# Revit family: QF_BOURGEAT_silo_encastrable_modele_rond_assiettes260
name_source: partatom
category: Equipement spécialisé
revit_build: Autodesk Revit 2015 (Build: 20140606_1530(x64)
units: mm (PartAtom-declared; Revit-internal decimal feet)

## types (2) — shared parameters
Charge max = 70.00 kg
Fabricant = BOURGEAT
Hauteur hors tout = 883 mm  [stored 2.89698 ft]
Longueur hors tout = 355 mm
Poids net à vide = 9.00 kg
Profondeur hors tout = 355 mm
Spécification du Fabricant = SILO A NIVEAU CONSTANT ENCASTRABLE
URL catalogue = http://www.bourgeat.fr
diag_const = 369 mm
larg_const = 325 mm  [stored 1.06627 ft]
prof_const = 325 mm  [stored 1.06627 ft]

## per-type parameters (varying)
| type | Fréquence | Indice de protection | Intensité nominale | Modèle | Phase | Puissance électrique  | Tension |
| silo_rond_assiettes260_chauffant_non_ventile | 50 Hz | 21 | 4 A | 777431 | 2 | 900 W | 230 V |
| silo_rond_assiettes260_neutre | 0 Hz | 0 | 0 A | 777432 | 0 | 0 W | 0 V |

note: [stored X ft] marks values corroborated as IEEE doubles in the binary element streams (Revit-internal decimal feet)
